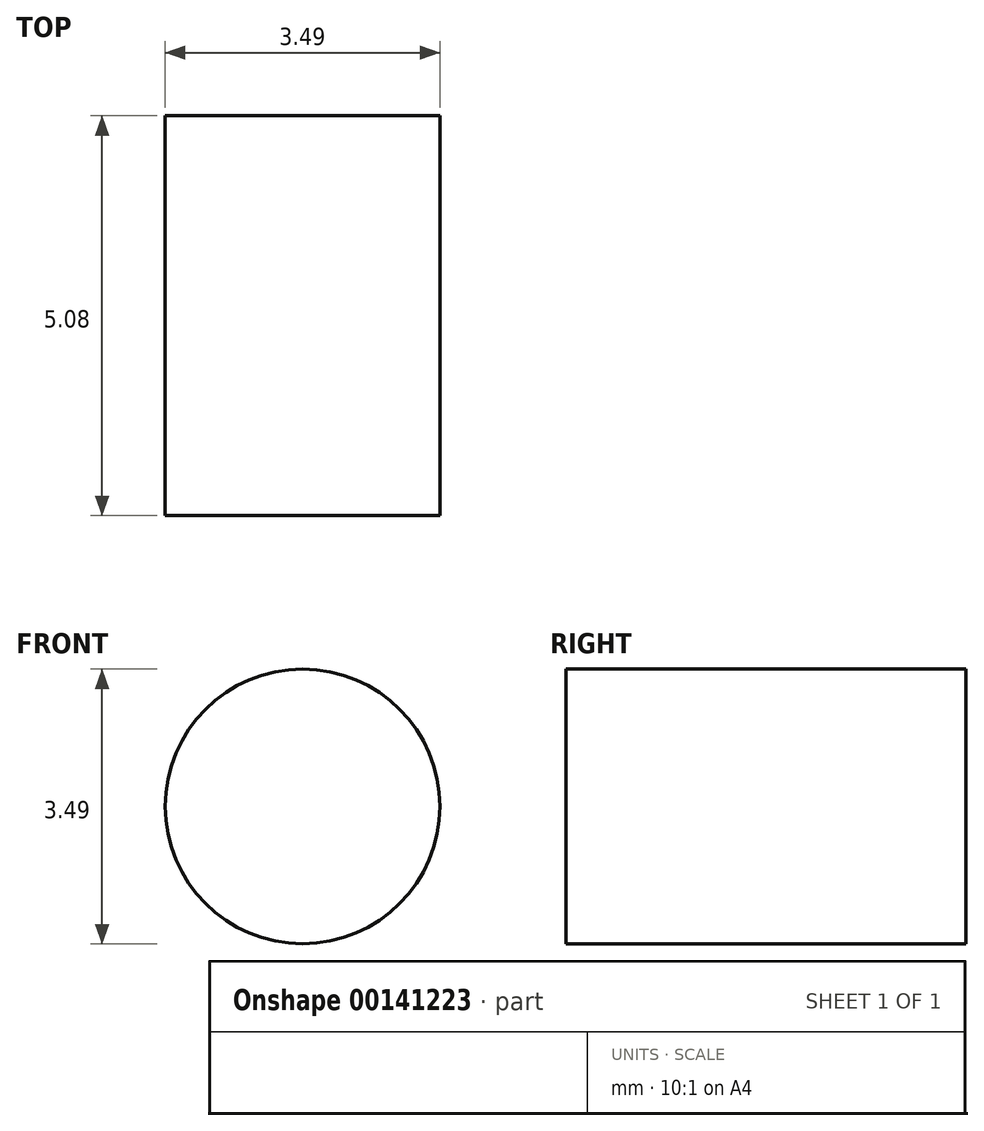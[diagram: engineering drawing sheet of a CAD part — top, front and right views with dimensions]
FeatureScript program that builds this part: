
annotation { "Feature Type Name" : "Feature", "Feature Type Description" : "" }
export const myFeature = defineFeature(function(context is Context, id is Id, definition is map)
    precondition{}
    {
        {
            var Q0;
            Q0=qCreatedBy(makeId("Front.planeOp"),FACE);
            var sketch = newSketch(context, id + "F0", { "sketchPlane" : qUnion([Q0])});
            skCircle(sketch, "E0", {"center": v(-33.36, 22.67) * mm, "radius": 1.74 * mm});
            skSolve(sketch);
        }
        {
            var Q0;
            Q0 = qSketchRegion(id + "F0", true);
            extrude(context, id + "F1", {"entities" : qUnion([Q0]), "depth" : 5.08 * mm});
        }
    });
